# Revit family: Furniture_Other_Sjobergs_Sewing_Table
name_source: partatom
category: Furniture
revit_build: Autodesk Revit 2017 (Build: 20190508_0315(x64)
units: mm (PartAtom-declared; Revit-internal decimal feet)

## family parameters
Always vertical = Yes
Cut with Voids When Loaded = No
OmniClass Number = 23.40.50.11
OmniClass Title = Educational, Entertainment Equipment and Furnishings
Room Calculation Point = No
Shared = No
Work Plane-Based = No

## types (1)
- Sewing Table
    AssetType = Movable
    BIMObjectName = Furniture_Other_Sjobergs_Sewing_Table
    Brand = Sjöbergs
    Category = School, textile craft
    Color = Wooden
    ConvergoRefNr = 0184-2005-0009-SE
    Cost = 0 $
    IfcExportAs = IfcFurnishingElementType
    IfcExportType = TABLE
    MainColor = Wooden
    ManufacterURL = https://www.sjobergs.se
    Manufacturer = Sjöbergs
    ManufacturerName = Sjöbergs
    Material = Wood
    Model = Sewing Table
    ModelNumber = 33064
    Name = Sjobergs_Sewing_Table
    NominalDepth = 600 mm  [stored 1.9685 ft]
    NominalHeight = 897 mm
    NominalWidth = 1200 mm
    ProductDatasheet = https://www.sjobergs.se
    ProductInformation = A complete sewing machine table consisting of table top 33105 in grey laminate. Legs 33106 in beech. Footboard in grey laminate. Cable channel 33212 and extension cord 33213 are included.
    SewingTableMainMaterial = Beech
    SewingTableSecondaryMaterial = Grey laminate
    Shape = Rectangular
    Size = 600x1200x897 mm
    URL = https://www.sjobergs.se
    Version = 1
    VersionDate = 30/06/2020
    Weight = 48 kg

note: [stored X ft] marks values corroborated as IEEE doubles in the binary element streams (Revit-internal decimal feet)

## geometry (parser evidence)
native form markers: Sweep x5
no freeform markers — native parametric forms only
